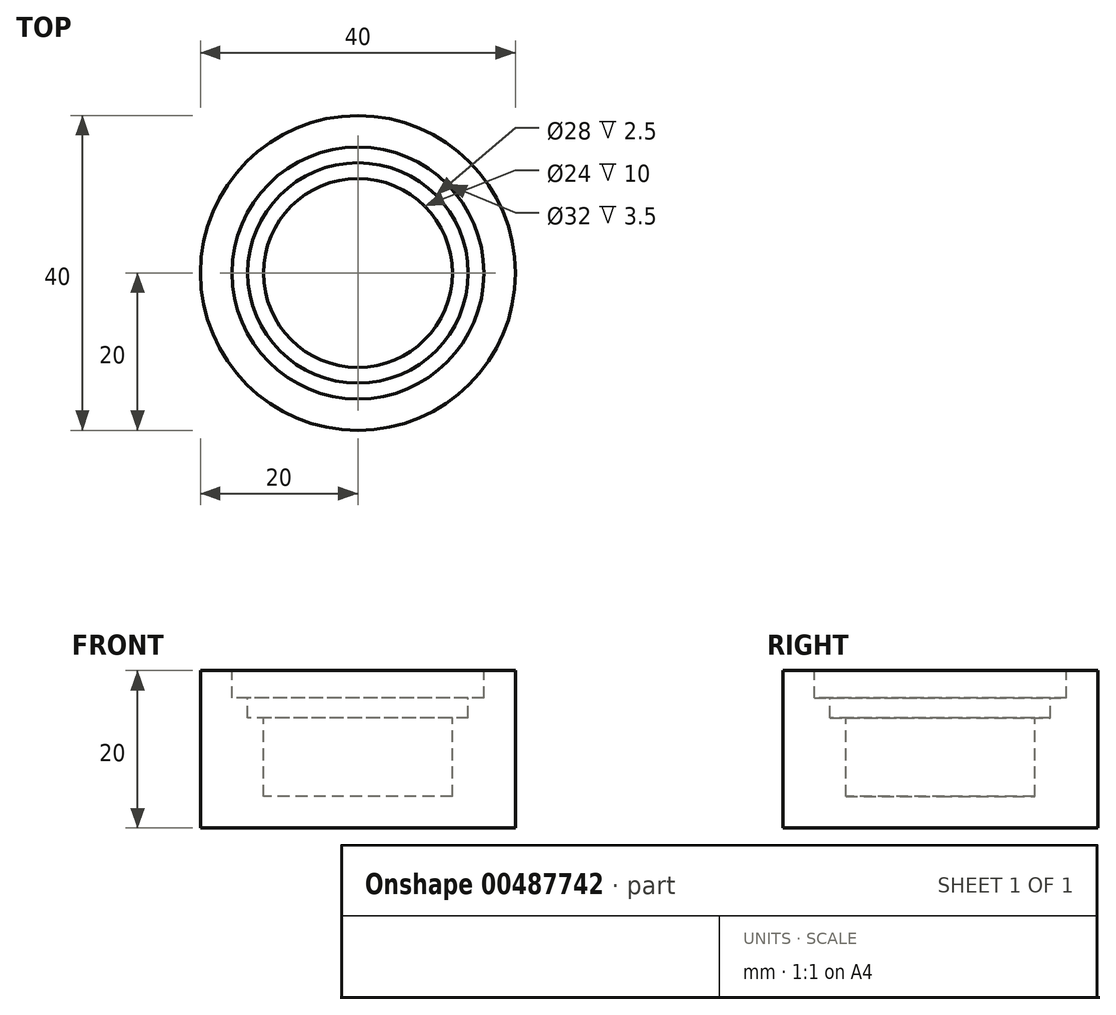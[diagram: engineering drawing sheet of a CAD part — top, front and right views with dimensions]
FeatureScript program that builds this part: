
annotation { "Feature Type Name" : "Feature", "Feature Type Description" : "" }
export const myFeature = defineFeature(function(context is Context, id is Id, definition is map)
    precondition{}
    {
        {
            var Q0;
            Q0=qCreatedBy(makeId("Top.planeOp"),FACE);
            var sketch = newSketch(context, id + "F0", { "sketchPlane" : qUnion([Q0])});
            skCircle(sketch, "E0", {"center": v(0, 0) * mm, "radius": 20 * mm});
            skCircle(sketch, "E1", {"center": v(0, 0) * mm, "radius": 12 * mm});
            skCircle(sketch, "E2", {"center": v(0, 0) * mm, "radius": 14 * mm});
            skCircle(sketch, "E3", {"center": v(0, 0) * mm, "radius": 16 * mm});
            skSolve(sketch);
        }
        {
            var Q0;
            Q0=makeQuery(id+"F0.imprint","IMPRINT",FACE,{"disambiguationData":[TD([[makeQuery(id+"F0.imprint","IMPRINT",EDGE,{"derivedFrom":sQuery(id+"F0.wireOp",EDGE,"E0")}),1.0]])]});
            var Q1;
            Q1=makeQuery(id+"F0.imprint","IMPRINT",FACE,{"disambiguationData":[TD([[makeQuery(id+"F0.imprint","IMPRINT",EDGE,{"derivedFrom":sQuery(id+"F0.wireOp",EDGE,"E2")}),-1.0]])]});
            var Q2;
            Q2=makeQuery(id+"F0.imprint","IMPRINT",FACE,{"disambiguationData":[TD([[makeQuery(id+"F0.imprint","IMPRINT",EDGE,{"derivedFrom":sQuery(id+"F0.wireOp",EDGE,"E1")}),-1.0]])]});
            var Q3;
            Q3=makeQuery(id+"F0.imprint","IMPRINT",FACE,{"disambiguationData":[TD([[makeQuery(id+"F0.imprint","IMPRINT",EDGE,{"derivedFrom":sQuery(id+"F0.wireOp",EDGE,"E1")}),1.0]])]});
            extrude(context, id + "F1", {"entities" : qUnion([Q0, Q1, Q2, Q3]), "oppositeDirection" : true, "depth" : 20 * mm});
        }
        {
            var Q0;
            Q0=makeQuery(id+"F0.imprint","IMPRINT",FACE,{"disambiguationData":[TD([[makeQuery(id+"F0.imprint","IMPRINT",EDGE,{"derivedFrom":sQuery(id+"F0.wireOp",EDGE,"E1")}),1.0]])]});
            extrude(context, id + "F2", {"entities" : qUnion([Q0]), "operationType" : NewBodyOperationType.REMOVE, "oppositeDirection" : true, "depth" : 16 * mm});
        }
        {
            var Q0;
            Q0=makeQuery(id+"F0.imprint","IMPRINT",FACE,{"disambiguationData":[TD([[makeQuery(id+"F0.imprint","IMPRINT",EDGE,{"derivedFrom":sQuery(id+"F0.wireOp",EDGE,"E1")}),-1.0]])]});
            extrude(context, id + "F3", {"entities" : qUnion([Q0]), "operationType" : NewBodyOperationType.REMOVE, "oppositeDirection" : true, "depth" : 6 * mm});
        }
        {
            var Q0;
            Q0=makeQuery(id+"F0.imprint","IMPRINT",FACE,{"disambiguationData":[TD([[makeQuery(id+"F0.imprint","IMPRINT",EDGE,{"derivedFrom":sQuery(id+"F0.wireOp",EDGE,"E2")}),-1.0]])]});
            extrude(context, id + "F4", {"entities" : qUnion([Q0]), "operationType" : NewBodyOperationType.REMOVE, "oppositeDirection" : true, "depth" : 3.5 * mm});
        }
    });
